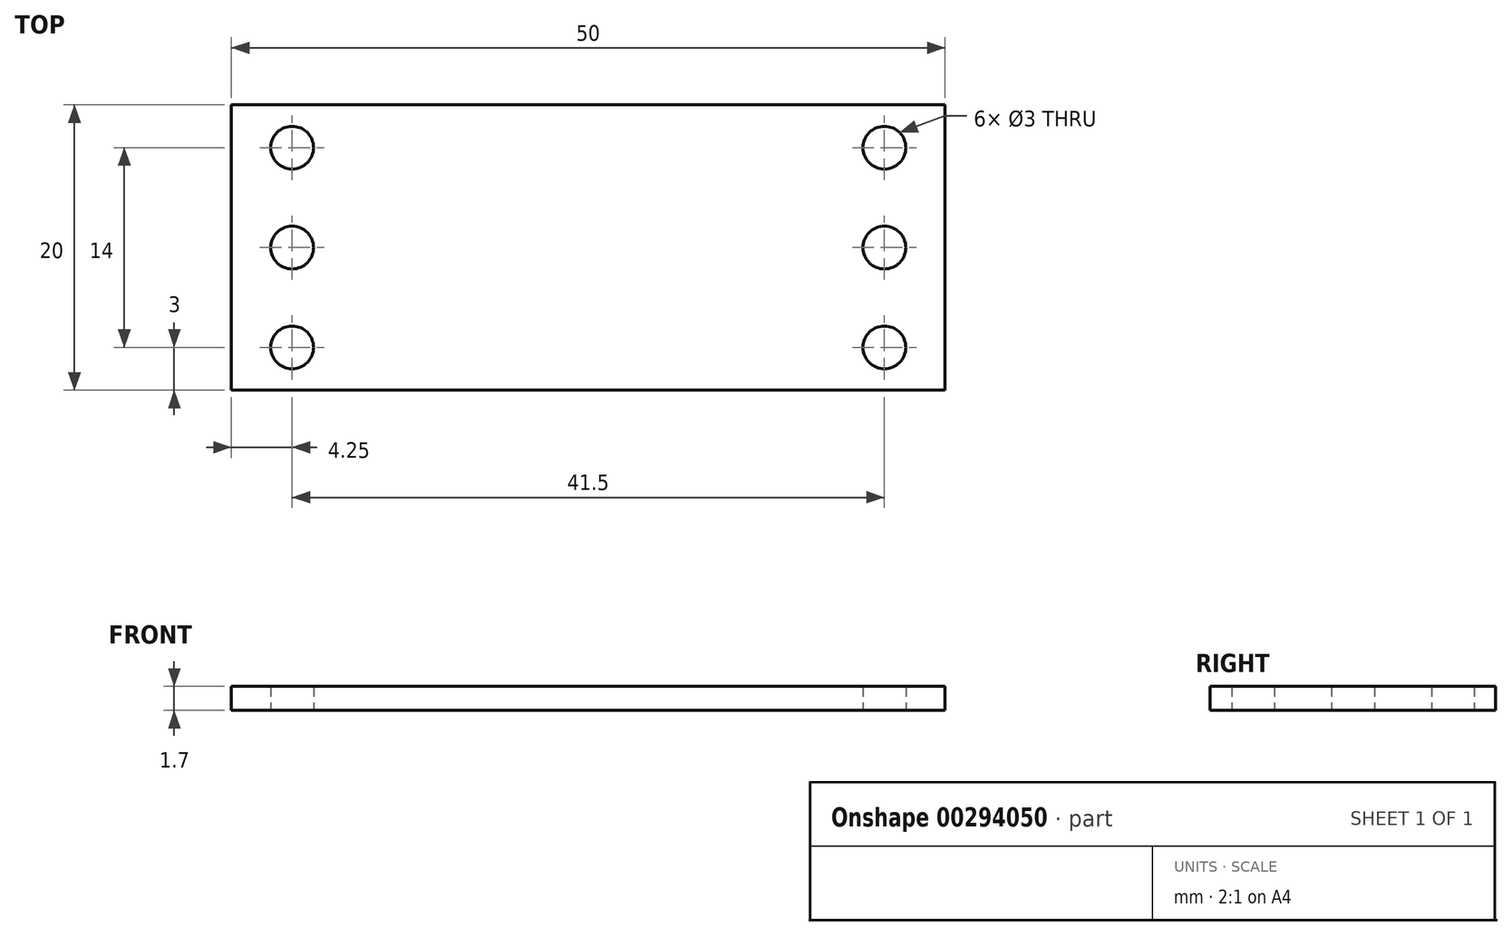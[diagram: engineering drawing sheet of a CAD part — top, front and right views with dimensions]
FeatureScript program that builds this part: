
annotation { "Feature Type Name" : "Feature", "Feature Type Description" : "" }
export const myFeature = defineFeature(function(context is Context, id is Id, definition is map)
    precondition{}
    {
        {
            var Q0;
            Q0=qCreatedBy(makeId("Top.planeOp"),FACE);
            var sketch = newSketch(context, id + "F0", { "sketchPlane" : qUnion([Q0])});
            skLineSegment(sketch, "E0.bottom", {"start": v(-25, -10) * mm, "end": v(25, -10) * mm});
            skLineSegment(sketch, "E0.top", {"start": v(-25, 10) * mm, "end": v(25, 10) * mm});
            skLineSegment(sketch, "E0.left", {"start": v(-25, -10) * mm, "end": v(-25, 10) * mm});
            skLineSegment(sketch, "E0.right", {"start": v(25, -10) * mm, "end": v(25, 10) * mm});
            skPoint(sketch, "E0.middle", {"position": v(0, 0) * mm});
            skLineSegment(sketch, "E1", {"start": v(0, 0) * mm, "end": v(0, 31.52) * mm, "construction": true});
            skCircle(sketch, "E2", {"center": v(-20.75, 0) * mm, "radius": 1.5 * mm});
            skLineSegment(sketch, "E3", {"start": v(-20.75, 0) * mm, "end": v(0, 0) * mm, "construction": true});
            skCircle(sketch, "E4", {"center": v(-20.75, 7) * mm, "radius": 1.5 * mm});
            skLineSegment(sketch, "E5", {"start": v(-20.75, 0) * mm, "end": v(-20.75, 7) * mm, "construction": true});
            skCircle(sketch, "E6.MirrorC", {"center": v(-20.75, -7) * mm, "radius": 1.5 * mm});
            skCircle(sketch, "E7.MirrorC", {"center": v(20.75, 7) * mm, "radius": 1.5 * mm});
            skCircle(sketch, "E8.MirrorC", {"center": v(20.75, 0) * mm, "radius": 1.5 * mm});
            skCircle(sketch, "E9.MirrorC", {"center": v(20.75, -7) * mm, "radius": 1.5 * mm});
            skSolve(sketch);
        }
        {
            var Q0;
            Q0 = qSketchRegion(id + "F0", true);
            extrude(context, id + "F1", {"entities" : qUnion([Q0]), "depth" : 1.7 * mm});
        }
    });
